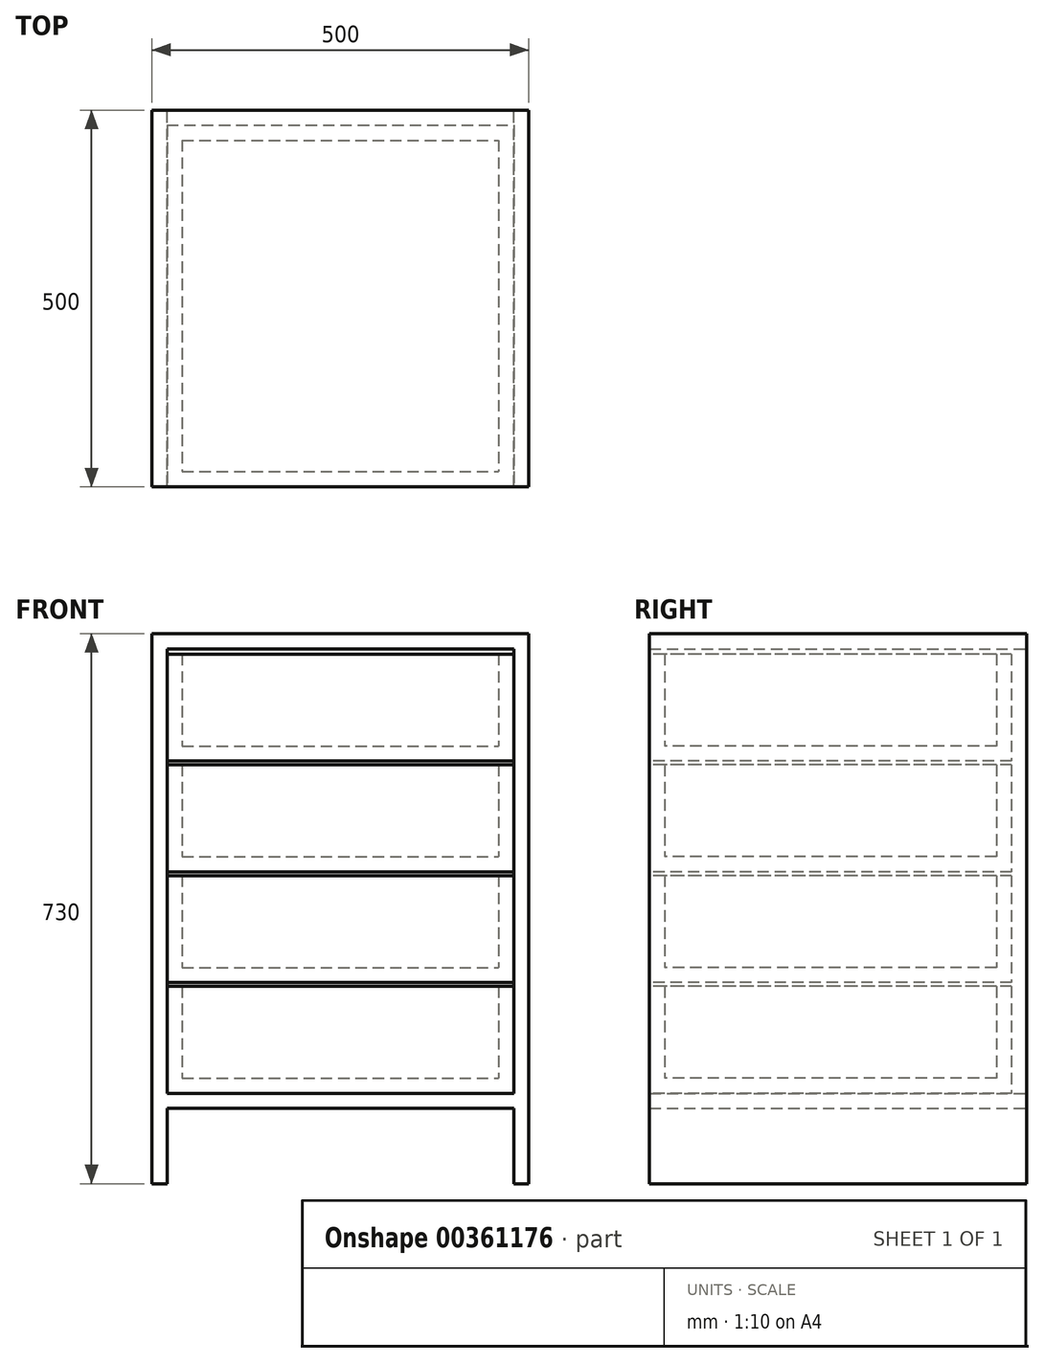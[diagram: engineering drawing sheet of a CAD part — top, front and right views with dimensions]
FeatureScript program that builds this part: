
annotation { "Feature Type Name" : "Feature", "Feature Type Description" : "" }
export const myFeature = defineFeature(function(context is Context, id is Id, definition is map)
    precondition{}
    {
        {
            var Q0;
            Q0=qCreatedBy(makeId("Front.planeOp"),FACE);
            var sketch = newSketch(context, id + "F0", { "sketchPlane" : qUnion([Q0])});
            skLineSegment(sketch, "E0", {"start": v(-38.2, 664.4) * mm, "end": v(-38.2, -45.6) * mm});
            skLineSegment(sketch, "E1", {"start": v(-38.2, -45.6) * mm, "end": v(-18.2, -45.6) * mm});
            skLineSegment(sketch, "E2.0", {"start": v(-18.2, 664.4) * mm, "end": v(-18.2, -45.6) * mm});
            skLineSegment(sketch, "E3", {"start": v(-38.2, 664.4) * mm, "end": v(-18.2, 664.4) * mm});
            skLineSegment(sketch, "E4", {"start": v(441.8, 664.4) * mm, "end": v(441.8, -45.6) * mm});
            skLineSegment(sketch, "E5", {"start": v(441.8, -45.6) * mm, "end": v(461.8, -45.6) * mm});
            skLineSegment(sketch, "E6.0", {"start": v(461.8, 664.4) * mm, "end": v(461.8, -45.6) * mm});
            skLineSegment(sketch, "E7", {"start": v(441.8, 664.4) * mm, "end": v(461.8, 664.4) * mm});
            skLineSegment(sketch, "E8", {"start": v(-38.2, 664.4) * mm, "end": v(-38.2, 684.4) * mm});
            skLineSegment(sketch, "E9", {"start": v(-38.2, 684.4) * mm, "end": v(461.8, 684.4) * mm});
            skLineSegment(sketch, "E10", {"start": v(461.8, 684.4) * mm, "end": v(461.8, 664.4) * mm});
            skLineSegment(sketch, "E11", {"start": v(-38.2, 664.4) * mm, "end": v(461.8, 664.4) * mm});
            skLineSegment(sketch, "E12", {"start": v(441.8, -45.6) * mm, "end": v(441.8, 54.4) * mm});
            skLineSegment(sketch, "E13", {"start": v(441.8, 54.4) * mm, "end": v(-18.2, 54.4) * mm});
            skLineSegment(sketch, "E14", {"start": v(-18.2, 54.4) * mm, "end": v(-18.2, 74.4) * mm});
            skLineSegment(sketch, "E15", {"start": v(-18.2, 74.4) * mm, "end": v(441.8, 74.4) * mm});
            skLineSegment(sketch, "E16", {"start": v(441.8, 74.4) * mm, "end": v(441.8, 54.4) * mm});
            skSolve(sketch);
        }
        {
            var Q0;
            Q0=makeQuery(id+"F0.imprint","IMPRINT",FACE,{"disambiguationData":[TD([[makeQuery(id+"F0.imprint","IMPRINT",EDGE,{"derivedFrom":sQuery(id+"F0.wireOp",EDGE,"E0")}),1.0]])]});
            var Q1;
            {var subQ1=sQuery(id+"F0.wireOp",EDGE,"E8");Q1=makeQuery(id+"F0.imprint","IMPRINT",FACE,{"disambiguationData":[TD([[makeQuery(id+"F0.imprint","IMPRINT",EDGE,{"derivedFrom":subQ1}),-1.0]])]});}
            var Q2;
            Q2=makeQuery(id+"F0.imprint","IMPRINT",FACE,{"disambiguationData":[TD([[makeQuery(id+"F0.imprint","IMPRINT",EDGE,{"derivedFrom":sQuery(id+"F0.wireOp",EDGE,"E13")}),-1.0]])]});
            var Q3;
            {var subQ1=sQuery(id+"F0.wireOp",EDGE,"E4");Q3=makeQuery(id+"F0.imprint","IMPRINT",FACE,{"disambiguationData":[TD([[makeQuery(id+"F0.imprint","IMPRINT",EDGE,{"derivedFrom":subQ1}),1.0]])]});}
            extrude(context, id + "F1", {"entities" : qUnion([Q0, Q1, Q2, Q3]), "depth" : 500 * mm});
        }
        {
            var Q0;
            Q0=makeQuery(id+"F1.opExtrude","CAP_FACE",FACE,{"disambiguationData":[OSD([sQuery(id+"F0.wireOp",EDGE,"E0"),sQuery(id+"F0.wireOp",EDGE,"E1"),sQuery(id+"F0.wireOp",EDGE,"E2.0"),sQuery(id+"F0.wireOp",EDGE,"E4"),sQuery(id+"F0.wireOp",EDGE,"E5"),sQuery(id+"F0.wireOp",EDGE,"E6.0"),sQuery(id+"F0.wireOp",EDGE,"E8"),sQuery(id+"F0.wireOp",EDGE,"E9"),sQuery(id+"F0.wireOp",EDGE,"E10"),sQuery(id+"F0.wireOp",EDGE,"E11"),sQuery(id+"F0.wireOp",EDGE,"E12"),sQuery(id+"F0.wireOp",EDGE,"E13"),sQuery(id+"F0.wireOp",EDGE,"E15")])],"isStart":false});
            var sketch = newSketch(context, id + "F2", { "sketchPlane" : qUnion([Q0])});
            skLineSegment(sketch, "E17", {"start": v(-18.2, 74.4) * mm, "end": v(441.8, 74.4) * mm});
            skLineSegment(sketch, "E18.0", {"start": v(-18.2, 216.4) * mm, "end": v(441.8, 216.4) * mm});
            skLineSegment(sketch, "E19.0", {"start": v(-18.2, 221.4) * mm, "end": v(441.8, 221.4) * mm});
            skLineSegment(sketch, "E20.0", {"start": v(-18.2, 363.4) * mm, "end": v(441.8, 363.4) * mm});
            skLineSegment(sketch, "E21.0", {"start": v(-18.2, 368.4) * mm, "end": v(441.8, 368.4) * mm});
            skLineSegment(sketch, "E22.0", {"start": v(-18.2, 510.4) * mm, "end": v(441.8, 510.4) * mm});
            skLineSegment(sketch, "E23.0", {"start": v(-18.2, 515.4) * mm, "end": v(441.8, 515.4) * mm});
            skLineSegment(sketch, "E24.0", {"start": v(-18.2, 657.4) * mm, "end": v(441.8, 657.4) * mm});
            skLineSegment(sketch, "E25", {"start": v(441.8, 657.4) * mm, "end": v(441.8, 515.4) * mm});
            skLineSegment(sketch, "E26", {"start": v(441.8, 510.4) * mm, "end": v(441.8, 368.4) * mm});
            skLineSegment(sketch, "E27", {"start": v(441.8, 363.4) * mm, "end": v(441.8, 221.4) * mm});
            skLineSegment(sketch, "E28", {"start": v(441.8, 216.4) * mm, "end": v(441.8, 74.4) * mm});
            skLineSegment(sketch, "E29", {"start": v(-18.2, 74.4) * mm, "end": v(-18.2, 216.4) * mm});
            skLineSegment(sketch, "E30", {"start": v(-18.2, 221.4) * mm, "end": v(-18.2, 363.4) * mm});
            skLineSegment(sketch, "E31", {"start": v(-18.2, 368.4) * mm, "end": v(-18.2, 510.4) * mm});
            skLineSegment(sketch, "E32", {"start": v(-18.2, 657.4) * mm, "end": v(-18.2, 515.4) * mm});
            skSolve(sketch);
        }
        {
            var Q0;
            Q0 = qSketchRegion(id + "F2", true);
            var Q1;
            Q1=makeQuery(id+"F2.imprint","IMPRINT",FACE,{"disambiguationData":[TD([[makeQuery(id+"F2.imprint","IMPRINT",EDGE,{"derivedFrom":sQuery(id+"F2.wireOp",EDGE,"E23.0")}),1.0]])]});
            var Q2;
            Q2=makeQuery(id+"F2.imprint","IMPRINT",FACE,{"disambiguationData":[TD([[makeQuery(id+"F2.imprint","IMPRINT",EDGE,{"derivedFrom":sQuery(id+"F2.wireOp",EDGE,"E21.0")}),1.0]])]});
            var Q3;
            Q3=makeQuery(id+"F2.imprint","IMPRINT",FACE,{"disambiguationData":[TD([[makeQuery(id+"F2.imprint","IMPRINT",EDGE,{"derivedFrom":sQuery(id+"F2.wireOp",EDGE,"E19.0")}),1.0]])]});
            var Q4;
            Q4=makeQuery(id+"F2.imprint","IMPRINT",FACE,{"disambiguationData":[TD([[makeQuery(id+"F2.imprint","IMPRINT",EDGE,{"derivedFrom":sQuery(id+"F2.wireOp",EDGE,"E17")}),1.0]])]});
            extrude(context, id + "F3", {"entities" : qUnion([Q0, Q1, Q2, Q3, Q4]), "oppositeDirection" : true, "depth" : 480 * mm});
        }
        {
            var Q0;
            Q0=makeQuery(id+"F3.opExtrude","SWEPT_FACE",FACE,{"disambiguationData":[OSD([sQuery(id+"F2.wireOp",EDGE,"E24.0")])]});
            var Q1;
            Q1=makeQuery(id+"F3.opExtrude","SWEPT_FACE",FACE,{"disambiguationData":[OSD([sQuery(id+"F2.wireOp",EDGE,"E22.0")])]});
            var Q2;
            Q2=makeQuery(id+"F3.opExtrude","SWEPT_FACE",FACE,{"disambiguationData":[OSD([sQuery(id+"F2.wireOp",EDGE,"E20.0")])]});
            var Q3;
            Q3=makeQuery(id+"F3.opExtrude","SWEPT_FACE",FACE,{"disambiguationData":[OSD([sQuery(id+"F2.wireOp",EDGE,"E18.0")])]});
            shell(context, id + "F4", {"entities" : qUnion([Q0, Q1, Q2, Q3]), "thickness" : 20 * mm});
        }
    });
